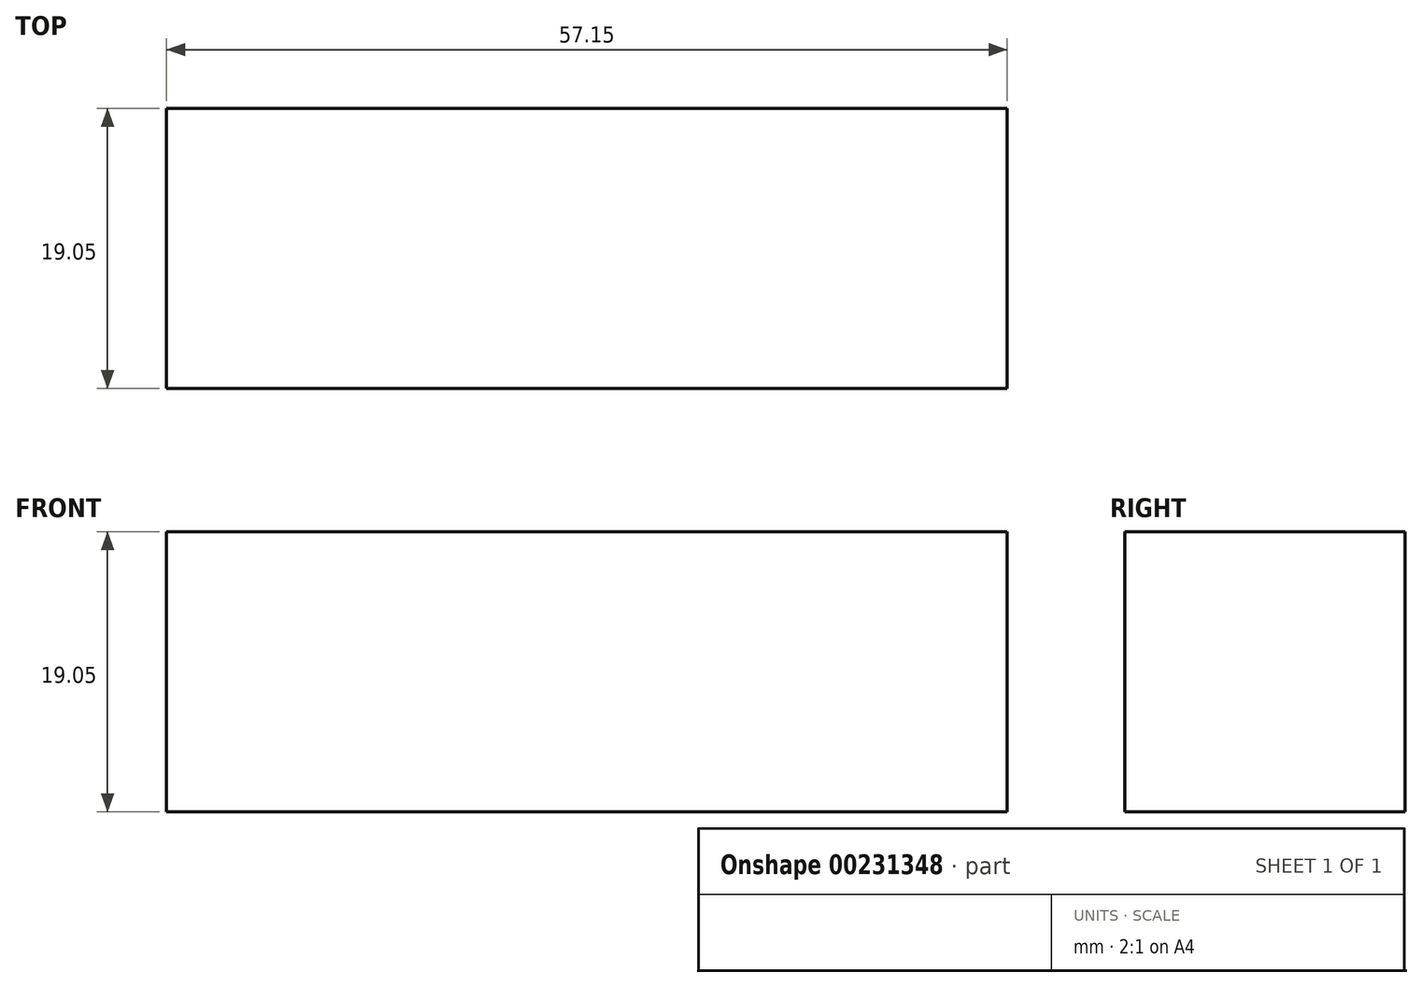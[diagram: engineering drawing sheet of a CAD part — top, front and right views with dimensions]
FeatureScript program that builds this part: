
annotation { "Feature Type Name" : "Feature", "Feature Type Description" : "" }
export const myFeature = defineFeature(function(context is Context, id is Id, definition is map)
    precondition{}
    {
        {
            var Q0;
            Q0=qCreatedBy(makeId("Front.planeOp"),FACE);
            var sketch = newSketch(context, id + "F0", { "sketchPlane" : qUnion([Q0])});
            skLineSegment(sketch, "E0.bottom", {"start": v(-72.92, 42.67) * mm, "end": v(-15.77, 42.67) * mm});
            skLineSegment(sketch, "E0.top", {"start": v(-72.92, 23.62) * mm, "end": v(-15.77, 23.62) * mm});
            skLineSegment(sketch, "E0.left", {"start": v(-72.92, 42.67) * mm, "end": v(-72.92, 23.62) * mm});
            skLineSegment(sketch, "E0.right", {"start": v(-15.77, 42.67) * mm, "end": v(-15.77, 23.62) * mm});
            skLineSegment(sketch, "E1.bottom", {"start": v(-53.01, 42.67) * mm, "end": v(-34.27, 42.67) * mm});
            skLineSegment(sketch, "E1.top", {"start": v(-53.01, 61.72) * mm, "end": v(-34.27, 61.72) * mm});
            skLineSegment(sketch, "E1.left", {"start": v(-53.01, 42.67) * mm, "end": v(-53.01, 61.72) * mm});
            skLineSegment(sketch, "E1.right", {"start": v(-34.27, 42.67) * mm, "end": v(-34.27, 61.72) * mm});
            skSolve(sketch);
        }
        {
            var Q0;
            Q0=makeQuery(id+"F0.imprint","IMPRINT",FACE,{"disambiguationData":[TD([[makeQuery(id+"F0.imprint","IMPRINT",EDGE,{"derivedFrom":sQuery(id+"F0.wireOp",EDGE,"E0.top")}),1.0]])]});
            var Q1;
            Q1=makeQuery(id+"F0.imprint","IMPRINT",FACE,{"disambiguationData":[TD([[makeQuery(id+"F0.imprint","IMPRINT",EDGE,{"derivedFrom":sQuery(id+"F0.wireOp",EDGE,"E1.bottom")}),1.0]])]});
            extrude(context, id + "F1", {"entities" : qUnion([Q0, Q1]), "depth" : 19.05 * mm});
        }
    });
